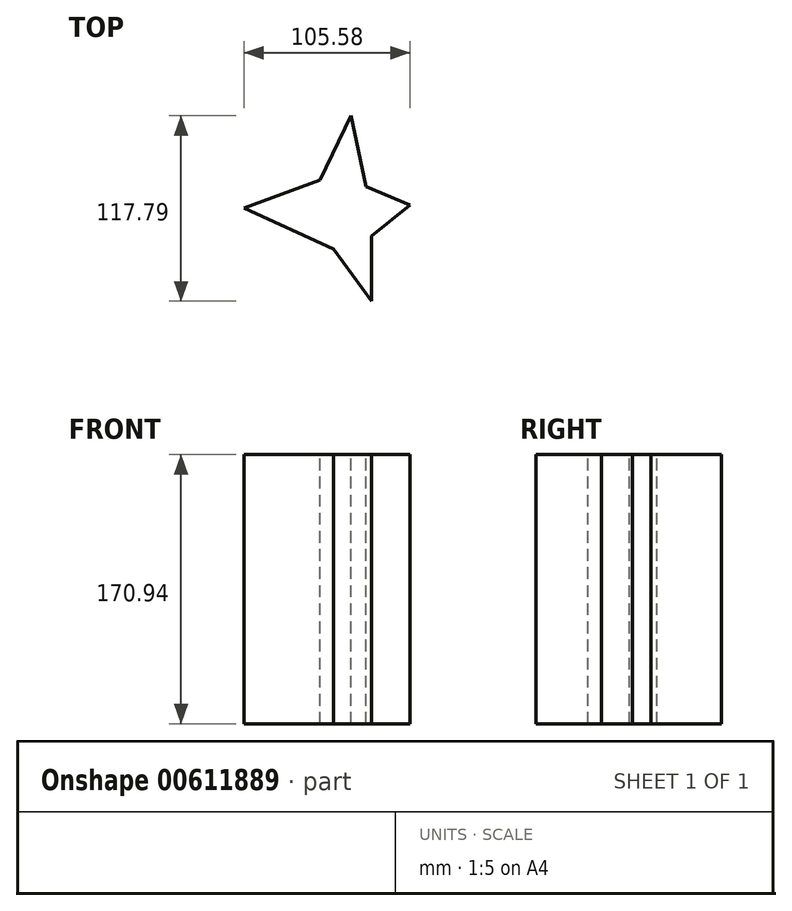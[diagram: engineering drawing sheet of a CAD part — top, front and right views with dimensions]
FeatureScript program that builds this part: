
annotation { "Feature Type Name" : "Feature", "Feature Type Description" : "" }
export const myFeature = defineFeature(function(context is Context, id is Id, definition is map)
    precondition{}
    {
        {
            var Q0;
            Q0=qCreatedBy(makeId("Top.planeOp"),FACE);
            var sketch = newSketch(context, id + "F0", { "sketchPlane" : qUnion([Q0])});
            skLineSegment(sketch, "E0", {"start": v(0, 0) * mm, "end": v(-56.91, 26.1) * mm});
            skLineSegment(sketch, "E1", {"start": v(-56.91, 26.1) * mm, "end": v(-8.5, 43.86) * mm});
            skLineSegment(sketch, "E2", {"start": v(-8.5, 43.86) * mm, "end": v(11.22, 84.76) * mm});
            skLineSegment(sketch, "E3", {"start": v(11.22, 84.76) * mm, "end": v(20.58, 39.91) * mm});
            skLineSegment(sketch, "E4", {"start": v(20.58, 39.91) * mm, "end": v(48.67, 28.09) * mm});
            skLineSegment(sketch, "E5", {"start": v(48.67, 28.09) * mm, "end": v(24.03, 8.37) * mm});
            skLineSegment(sketch, "E6", {"start": v(24.03, 8.37) * mm, "end": v(24.03, -33.03) * mm});
            skLineSegment(sketch, "E7", {"start": v(24.03, -33.03) * mm, "end": v(0, 0) * mm});
            skSolve(sketch);
        }
        {
            var Q0;
            Q0 = qSketchRegion(id + "F0", true);
            var Q1;
            Q1=makeQuery(id+"F0.imprint","IMPRINT",FACE,{"disambiguationData":[TD([[makeQuery(id+"F0.imprint","IMPRINT",EDGE,{"derivedFrom":sQuery(id+"F0.wireOp",EDGE,"E0")}),-1.0]])]});
            extrude(context, id + "F1", {"entities" : qUnion([Q0, Q1]), "oppositeDirection" : true, "depth" : 170.94 * mm, "offsetDistance" : 25.4 * mm});
        }
    });
